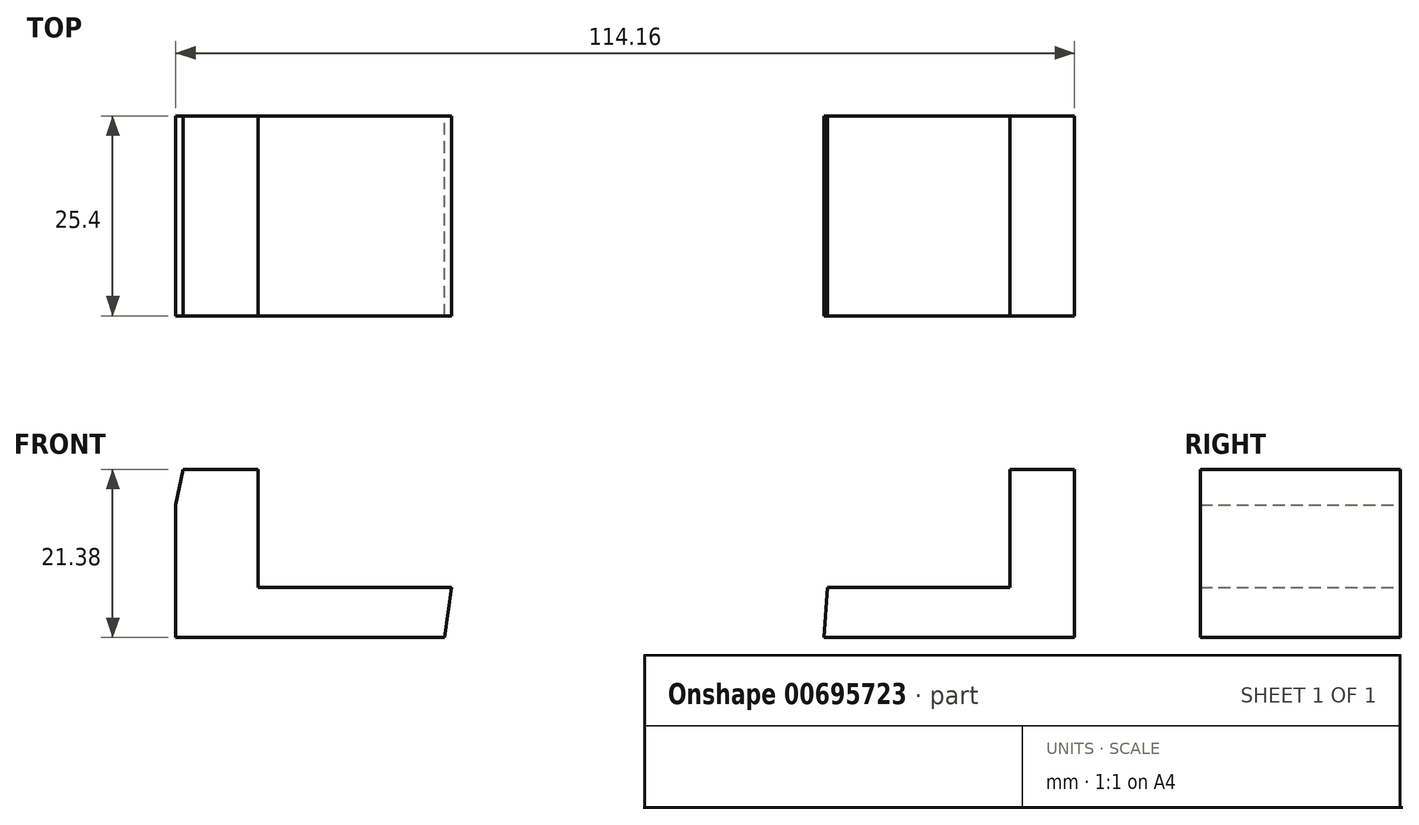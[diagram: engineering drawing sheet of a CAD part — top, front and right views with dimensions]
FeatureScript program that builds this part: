
annotation { "Feature Type Name" : "Feature", "Feature Type Description" : "" }
export const myFeature = defineFeature(function(context is Context, id is Id, definition is map)
    precondition{}
    {
        {
            var Q0;
            Q0=qCreatedBy(makeId("Front.planeOp"),FACE);
            var sketch = newSketch(context, id + "F0", { "sketchPlane" : qUnion([Q0])});
            skLineSegment(sketch, "E0", {"start": v(-124.85, 56.4) * mm, "end": v(-124.85, 39.57) * mm});
            skLineSegment(sketch, "E1", {"start": v(-124.85, 39.57) * mm, "end": v(-90.74, 39.57) * mm});
            skLineSegment(sketch, "E2", {"start": v(-42.53, 39.57) * mm, "end": v(-10.69, 39.57) * mm});
            skLineSegment(sketch, "E3", {"start": v(-10.69, 39.57) * mm, "end": v(-10.69, 60.95) * mm});
            skLineSegment(sketch, "E4", {"start": v(-10.69, 60.95) * mm, "end": v(-18.88, 60.95) * mm});
            skLineSegment(sketch, "E5", {"start": v(-18.88, 60.95) * mm, "end": v(-18.88, 45.94) * mm});
            skLineSegment(sketch, "E6", {"start": v(-114.39, 45.94) * mm, "end": v(-114.39, 60.95) * mm});
            skLineSegment(sketch, "E7", {"start": v(-114.39, 60.95) * mm, "end": v(-123.94, 60.95) * mm});
            skLineSegment(sketch, "E8", {"start": v(-123.94, 60.95) * mm, "end": v(-124.85, 56.4) * mm});
            skArc(sketch, "E9", {"start": v(-90.74, 39.57) * mm, "mid": v(-66.63, 17) * mm, "end": v(-42.53, 39.57) * mm});
            skLineSegment(sketch, "E10", {"start": v(-114.39, 45.94) * mm, "end": v(-89.83, 45.94) * mm});
            skLineSegment(sketch, "E11", {"start": v(-89.83, 45.94) * mm, "end": v(-90.74, 39.57) * mm});
            skLineSegment(sketch, "E12", {"start": v(-18.88, 45.94) * mm, "end": v(-42.07, 45.94) * mm});
            skLineSegment(sketch, "E13", {"start": v(-42.07, 45.94) * mm, "end": v(-42.53, 39.57) * mm});
            skSolve(sketch);
        }
        {
            var Q0;
            Q0 = qSketchRegion(id + "F0", true);
            extrude(context, id + "F1", {"entities" : qUnion([Q0]), "depth" : 25.4 * mm, "offsetDistance" : 25.4 * mm});
        }
    });
